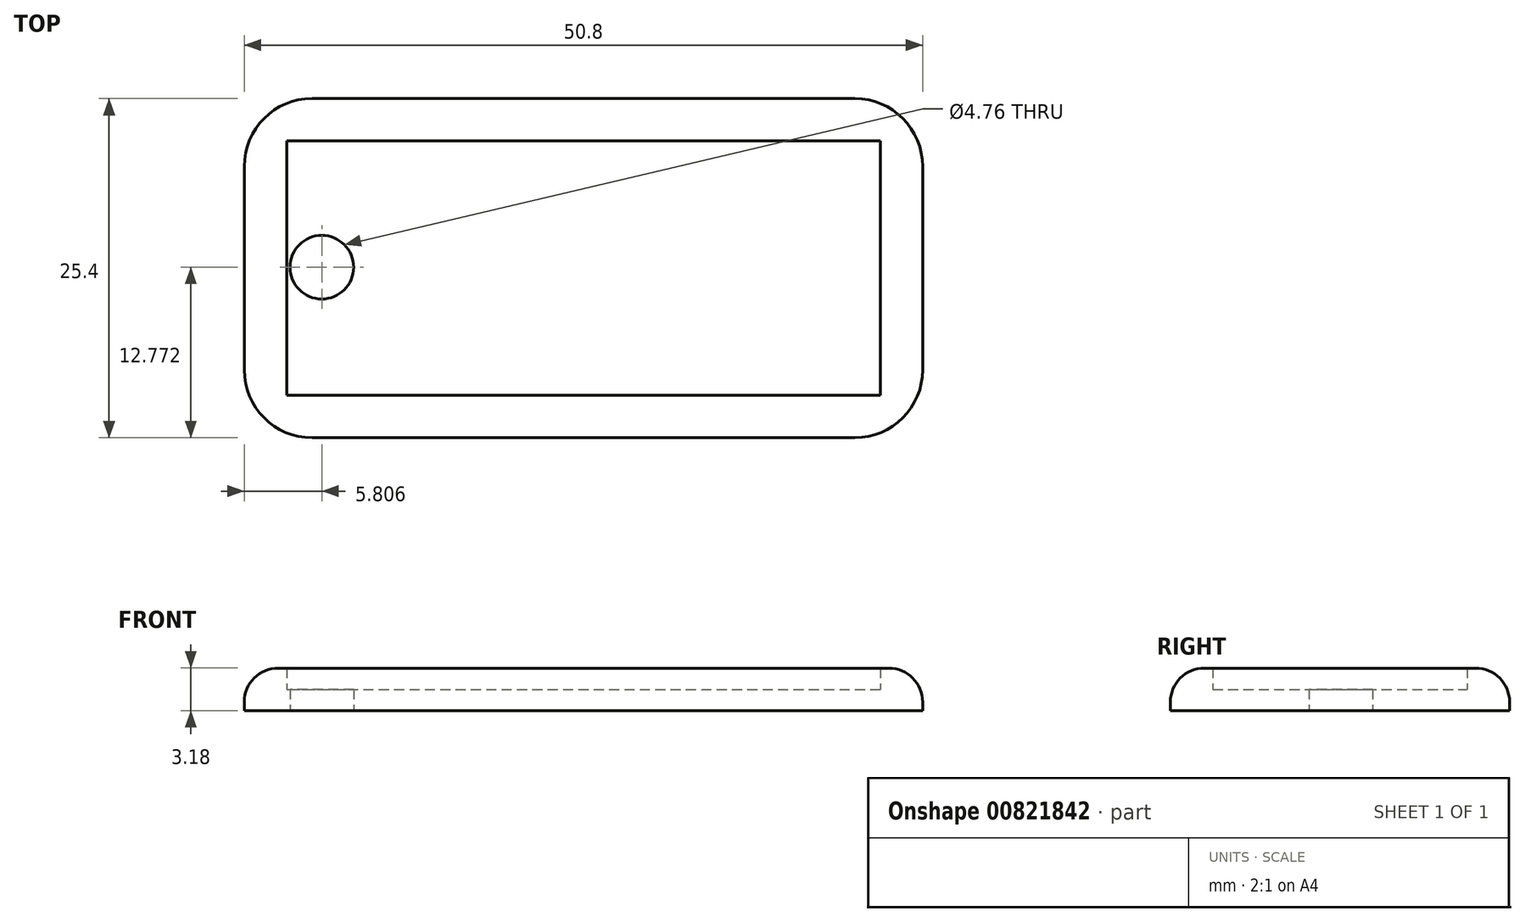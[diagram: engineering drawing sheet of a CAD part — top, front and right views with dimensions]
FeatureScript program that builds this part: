
annotation { "Feature Type Name" : "Feature", "Feature Type Description" : "" }
export const myFeature = defineFeature(function(context is Context, id is Id, definition is map)
    precondition{}
    {
        {
            var Q0;
            Q0=qCreatedBy(makeId("Top.planeOp"),FACE);
            var sketch = newSketch(context, id + "F0", { "sketchPlane" : qUnion([Q0])});
            skLineSegment(sketch, "E0.bottom", {"start": v(0, 0) * mm, "end": v(50.8, 0) * mm});
            skLineSegment(sketch, "E0.top", {"start": v(0, 25.4) * mm, "end": v(50.8, 25.4) * mm});
            skLineSegment(sketch, "E0.left", {"start": v(0, 0) * mm, "end": v(0, 25.4) * mm});
            skLineSegment(sketch, "E0.right", {"start": v(50.8, 0) * mm, "end": v(50.8, 25.4) * mm});
            skCircle(sketch, "E1", {"center": v(5.8, 12.77) * mm, "radius": 2.38 * mm});
            skLineSegment(sketch, "E2.0", {"start": v(3.17, 22.23) * mm, "end": v(47.62, 22.23) * mm});
            skLineSegment(sketch, "E2.1", {"start": v(3.18, 3.18) * mm, "end": v(3.17, 22.23) * mm});
            skLineSegment(sketch, "E2.2", {"start": v(3.18, 3.18) * mm, "end": v(47.62, 3.18) * mm});
            skLineSegment(sketch, "E2.3", {"start": v(47.62, 3.18) * mm, "end": v(47.62, 22.23) * mm});
            skSolve(sketch);
        }
        {
            var Q0;
            Q0=makeQuery(id+"F0.imprint","IMPRINT",FACE,{"disambiguationData":[TD([[makeQuery(id+"F0.imprint","IMPRINT",EDGE,{"derivedFrom":sQuery(id+"F0.wireOp",EDGE,"E1")}),-1.0]])]});
            extrude(context, id + "F1", {"entities" : qUnion([Q0]), "depth" : 1.59 * mm, "offsetDistance" : 25.4 * mm});
        }
        {
            var Q0;
            Q0 = qSketchRegion(id + "F0", true);
            extrude(context, id + "F2", {"entities" : qUnion([Q0]), "operationType" : NewBodyOperationType.ADD, "depth" : 3.17 * mm, "offsetDistance" : 25.4 * mm});
        }
        {
            var Q0;
            Q0=makeQuery(id+"F2.opExtrude","SWEPT_EDGE",EDGE,{"disambiguationData":[OSD([sQuery(id+"F0.wireOp",EDGE,"E0.bottom"),sQuery(id+"F0.wireOp",EDGE,"E0.left")])]});
            var Q1;
            Q1=makeQuery(id+"F2.opExtrude","SWEPT_EDGE",EDGE,{"disambiguationData":[OSD([sQuery(id+"F0.wireOp",EDGE,"E0.bottom"),sQuery(id+"F0.wireOp",EDGE,"E0.right")])]});
            var Q2;
            Q2=makeQuery(id+"F2.opExtrude","SWEPT_EDGE",EDGE,{"disambiguationData":[OSD([sQuery(id+"F0.wireOp",EDGE,"E0.top"),sQuery(id+"F0.wireOp",EDGE,"E0.right")])]});
            var Q3;
            Q3=makeQuery(id+"F2.opExtrude","SWEPT_EDGE",EDGE,{"disambiguationData":[OSD([sQuery(id+"F0.wireOp",EDGE,"E0.top"),sQuery(id+"F0.wireOp",EDGE,"E0.left")])]});
            fillet(context, id + "F3", {"entities" : qUnion([Q0, Q1, Q2, Q3]), "radius" : 5.08 * mm, "tangentPropagation" : true, "allowEdgeOverflow" : false});
        }
        {
            var Q0;
            Q0=makeQuery(id+"F2.opExtrude","CAP_EDGE",EDGE,{"disambiguationData":[OSD([sQuery(id+"F0.wireOp",EDGE,"E0.bottom")])],"isStart":false});
            fillet(context, id + "F4", {"entities" : qUnion([Q0]), "radius" : 2.54 * mm, "tangentPropagation" : true, "allowEdgeOverflow" : false});
        }
        {
            var Q0;
            Q0=qCreatedBy(makeId("Top.planeOp"),FACE);
            var sketch = newSketch(context, id + "F5", { "sketchPlane" : qUnion([Q0])});
            skText(sketch, "E3", { "text": "Cassidy\n\n\n", "fontName": "OpenSans-Regular.ttf"});
            const initialGuessF5  = {"E3": [0.00797, 0.0088, 1, 0, 0.00767]};
            skSetInitialGuess(sketch, initialGuessF5);
            skSolve(sketch);
        }
        {
            var Q0;
            Q0 = qSketchRegion(id + "F5", true);
            extrude(context, id + "F6", {"entities" : qUnion([Q0]), "operationType" : NewBodyOperationType.ADD, "depth" : 0.8 * mm, "offsetDistance" : 25.4 * mm});
        }
    });
